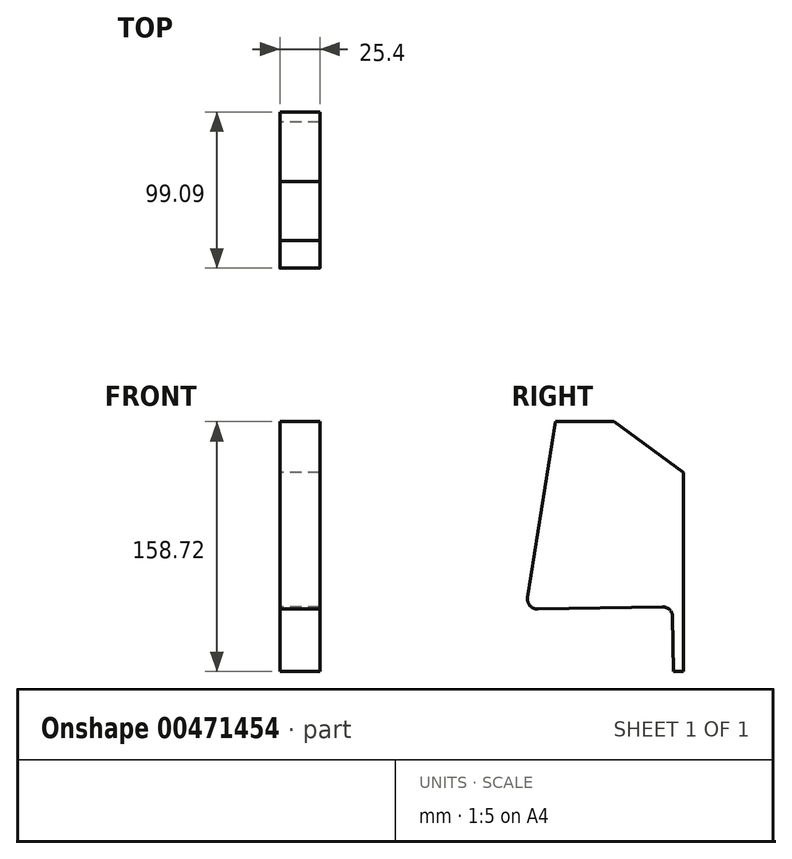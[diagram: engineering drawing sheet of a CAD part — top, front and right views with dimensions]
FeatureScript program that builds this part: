
annotation { "Feature Type Name" : "Feature", "Feature Type Description" : "" }
export const myFeature = defineFeature(function(context is Context, id is Id, definition is map)
    precondition{}
    {
        {
            var Q0;
            Q0=qCreatedBy(makeId("Right.planeOp"),FACE);
            var sketch = newSketch(context, id + "F0", { "sketchPlane" : qUnion([Q0])});
            skLineSegment(sketch, "E0", {"start": v(-13.45, 64.21) * mm, "end": v(-50.9, 64.21) * mm});
            skLineSegment(sketch, "E1", {"start": v(-50.9, 64.21) * mm, "end": v(-68.42, -47.57) * mm});
            skLineSegment(sketch, "E2", {"start": v(-62.03, -54.9) * mm, "end": v(17.14, -53.44) * mm});
            skLineSegment(sketch, "E3", {"start": v(23.6, -59.67) * mm, "end": v(24.25, -94.51) * mm});
            skLineSegment(sketch, "E4", {"start": v(24.25, -94.51) * mm, "end": v(30.59, -94.51) * mm});
            skLineSegment(sketch, "E5", {"start": v(30.59, -94.51) * mm, "end": v(30.59, 31.87) * mm});
            skLineSegment(sketch, "E6", {"start": v(30.59, 31.87) * mm, "end": v(-13.45, 64.21) * mm});
            skPoint(sketch, "E7.visualSharp", {"position": v(23.49, -53.32) * mm});
            skArc(sketch, "E7.filletArc", {"start": v(23.6, -59.67) * mm, "mid": v(21.66, -55.21) * mm, "end": v(17.14, -53.44) * mm});
            skPoint(sketch, "E8.visualSharp", {"position": v(-69.6, -55.04) * mm});
            skArc(sketch, "E8.filletArc", {"start": v(-68.42, -47.57) * mm, "mid": v(-66.94, -52.72) * mm, "end": v(-62.03, -54.9) * mm});
            skSolve(sketch);
        }
        {
            var Q0;
            Q0=makeQuery(id+"F0.imprint","IMPRINT",FACE,{"disambiguationData":[TD([[makeQuery(id+"F0.imprint","IMPRINT",EDGE,{"derivedFrom":sQuery(id+"F0.wireOp",EDGE,"E0")}),1.0]])]});
            extrude(context, id + "F1", {"entities" : qUnion([Q0]), "depth" : 25.4 * mm});
        }
        {
            var Q0;
            Q0=makeQuery(id+"F1.opExtrude","CAP_FACE",FACE,{"disambiguationData":[OSD([sQuery(id+"F0.wireOp",EDGE,"E0"),sQuery(id+"F0.wireOp",EDGE,"E1"),sQuery(id+"F0.wireOp",EDGE,"E2"),sQuery(id+"F0.wireOp",EDGE,"E3"),sQuery(id+"F0.wireOp",EDGE,"E4"),sQuery(id+"F0.wireOp",EDGE,"E5"),sQuery(id+"F0.wireOp",EDGE,"E6"),sQuery(id+"F0.wireOp",EDGE,"E7.filletArc"),sQuery(id+"F0.wireOp",EDGE,"E8.filletArc")])],"isStart":true});
            var sketch = newSketch(context, id + "F2", { "sketchPlane" : qUnion([Q0])});
            skLineSegment(sketch, "E9", {"start": v(11.63, 53.07) * mm, "end": v(45.87, 53.07) * mm});
            skLineSegment(sketch, "E10", {"start": v(45.87, 53.07) * mm, "end": v(54.3, 0) * mm});
            skLineSegment(sketch, "E11", {"start": v(11.63, 53.07) * mm, "end": v(-21.92, 23) * mm});
            skLineSegment(sketch, "E12", {"start": v(-21.92, 23) * mm, "end": v(54.3, 0) * mm});
            skSolve(sketch);
        }
        {
            var Q0;
            Q0=makeQuery(id+"F2.imprint","IMPRINT",FACE,{"disambiguationData":[TD([[makeQuery(id+"F2.imprint","IMPRINT",EDGE,{"derivedFrom":sQuery(id+"F2.wireOp",EDGE,"E9")}),-1.0]])]});
            var Q1;
            Q1=sQuery(id+"F2.wireOp",EDGE,"E12");
            var Q2;
            Q2=sQuery(id+"F2.wireOp",EDGE,"E10");
            var Q3;
            Q3=sQuery(id+"F2.wireOp",EDGE,"E9");
            var Q4;
            Q4=sQuery(id+"F2.wireOp",EDGE,"E11");
            extrude(context, id + "F3", {"entities" : qUnion([Q0]), "bodyType" : ToolBodyType.SURFACE, "surfaceEntities" : qUnion([Q1, Q2, Q3, Q4]), "endBound" : BoundingType.UP_TO_NEXT, "oppositeDirection" : true, "depth" : 25.4 * mm});
        }
    });
